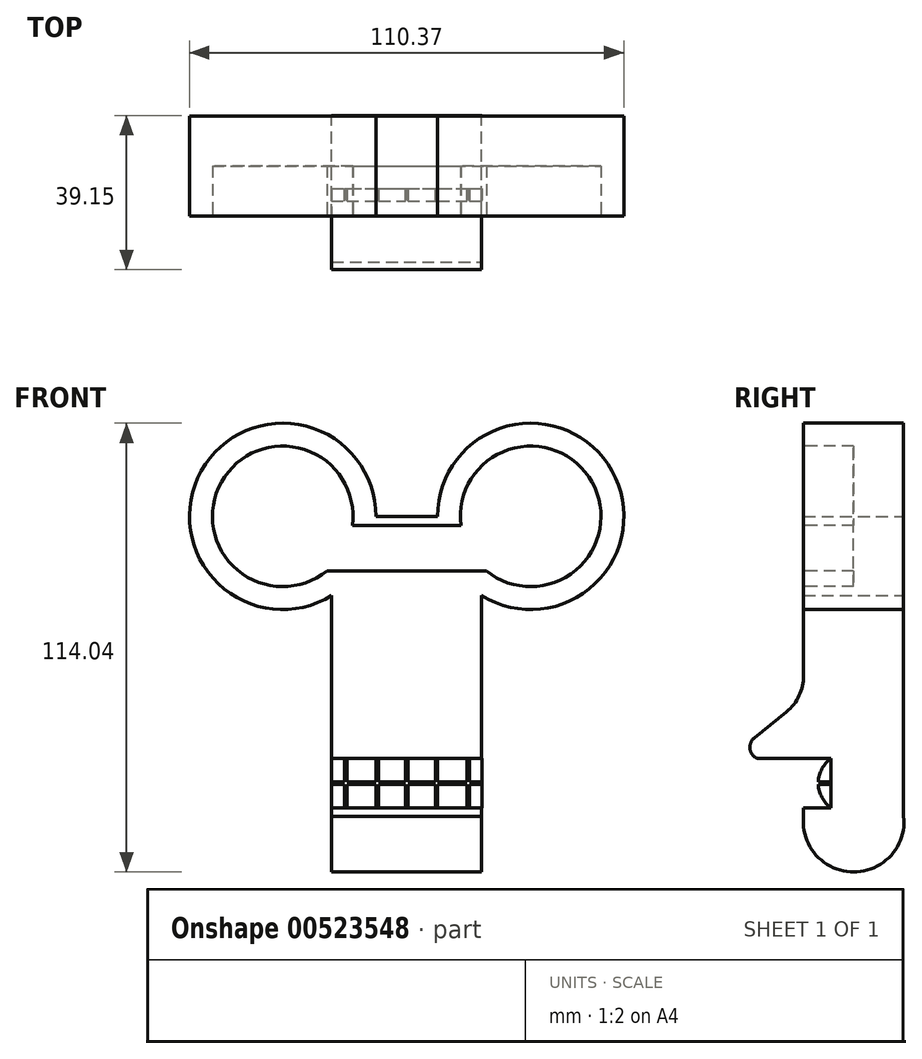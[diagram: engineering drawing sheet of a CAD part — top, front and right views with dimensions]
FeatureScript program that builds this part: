
annotation { "Feature Type Name" : "Feature", "Feature Type Description" : "" }
export const myFeature = defineFeature(function(context is Context, id is Id, definition is map)
    precondition{}
    {
        {
            var Q0;
            Q0=qCreatedBy(makeId("Front.planeOp"),FACE);
            var sketch = newSketch(context, id + "F0", { "sketchPlane" : qUnion([Q0])});
            skLineSegment(sketch, "E0.bottom", {"start": v(-13.77, 56.32) * mm, "end": v(1.87, 56.32) * mm});
            skLineSegment(sketch, "E0.top", {"start": v(-25, -19.88) * mm, "end": v(13.1, -19.88) * mm});
            skLineSegment(sketch, "E0.left", {"start": v(-25, 36.18) * mm, "end": v(-25, -19.88) * mm});
            skLineSegment(sketch, "E0.right", {"start": v(13.1, 36.17) * mm, "end": v(13.1, -19.88) * mm});
            skArc(sketch, "E1", {"start": v(-13.77, 56.32) * mm, "mid": v(-58.14, 67.85) * mm, "end": v(-25, 36.18) * mm});
            skArc(sketch, "E2", {"start": v(13.1, 36.17) * mm, "mid": v(46.23, 67.85) * mm, "end": v(1.87, 56.32) * mm});
            skPoint(sketch, "E3.orphan", {"position": v(-25, 56.32) * mm});
            skPoint(sketch, "E4.orphan", {"position": v(13.1, 56.32) * mm});
            skArc(sketch, "E5", {"start": v(-19.76, 54.02) * mm, "mid": v(-53.04, 65.01) * mm, "end": v(-26.2, 42.48) * mm});
            skArc(sketch, "E6", {"start": v(14.28, 42.48) * mm, "mid": v(41.14, 65.01) * mm, "end": v(7.85, 54.02) * mm});
            skLineSegment(sketch, "E7", {"start": v(-19.76, 54.02) * mm, "end": v(7.85, 54.02) * mm});
            skLineSegment(sketch, "E8", {"start": v(-26.2, 42.48) * mm, "end": v(14.28, 42.48) * mm});
            skSolve(sketch);
        }
        {
            var Q0;
            Q0 = qSketchRegion(id + "F0", true);
            var Q1;
            Q1=makeQuery(id+"F0.imprint","IMPRINT",FACE,{"disambiguationData":[TD([[makeQuery(id+"F0.imprint","IMPRINT",EDGE,{"derivedFrom":sQuery(id+"F0.wireOp",EDGE,"E5")}),1.0]])]});
            extrude(context, id + "F1", {"entities" : qUnion([Q0, Q1]), "depth" : 25.4 * mm, "offsetDistance" : 25.4 * mm});
        }
        {
            var Q0;
            Q0=makeQuery(id+"F1.opExtrude","SWEPT_FACE",FACE,{"disambiguationData":[OSD([sQuery(id+"F0.wireOp",EDGE,"E0.right")])]});
            var sketch = newSketch(context, id + "F2", { "sketchPlane" : qUnion([Q0])});
            skArc(sketch, "E9", {"start": v(-25.4, -19.88) * mm, "mid": v(-12.7, -34.04) * mm, "end": v(0, -19.88) * mm});
            skSolve(sketch);
        }
        {
            var Q0;
            Q0=makeQuery(id+"F2.imprint","IMPRINT",FACE,{"disambiguationData":[TD([[makeQuery(id+"F2.imprint","IMPRINT",EDGE,{"derivedFrom":sQuery(id+"F2.wireOp",EDGE,"E9")}),1.0]])]});
            var Q1;
            Q1=makeQuery(id+"F1.opExtrude","SWEPT_FACE",FACE,{"disambiguationData":[OSD([sQuery(id+"F0.wireOp",EDGE,"E0.left")])]});
            extrude(context, id + "F3", {"entities" : qUnion([Q0]), "operationType" : NewBodyOperationType.ADD, "endBound" : BoundingType.UP_TO_SURFACE, "oppositeDirection" : true, "depth" : 25.4 * mm, "endBoundEntityFace" : qUnion([Q1]), "offsetDistance" : 25.4 * mm});
        }
        {
            var Q0;
            {var subQ0=sQuery(id+"F0.wireOp",EDGE,"E0.right");Q0=makeQuery(id+"F3.boolean.opBoolean","MERGE",FACE,{"derivedFrom":[makeQuery(id+"F1.opExtrude","SWEPT_FACE",FACE,{"disambiguationData":[OSD([subQ0])]}),makeQuery(id+"F3.opExtrude","CAP_FACE",FACE,{"disambiguationData":[OSD([sQuery(id+"F0.wireOp",EDGE,"E0.top"),subQ0,sQuery(id+"F2.wireOp",EDGE,"E9")])],"isStart":true})]});}
            var sketch = newSketch(context, id + "F4", { "sketchPlane" : qUnion([Q0])});
            skLineSegment(sketch, "E10", {"start": v(-25.4, 10.2) * mm, "end": v(-37.94, 0) * mm});
            skArc(sketch, "E11", {"start": v(-37.94, 0) * mm, "mid": v(-39.04, -2.8) * mm, "end": v(-37.2, -5.18) * mm});
            skLineSegment(sketch, "E12", {"start": v(-37.2, -5.18) * mm, "end": v(-25.4, -5.18) * mm});
            skLineSegment(sketch, "E13.bottom", {"start": v(-25.4, -5.18) * mm, "end": v(-18.41, -5.18) * mm});
            skLineSegment(sketch, "E13.top", {"start": v(-25.4, -17.75) * mm, "end": v(-18.41, -17.75) * mm});
            skLineSegment(sketch, "E13.left", {"start": v(-25.4, -5.18) * mm, "end": v(-25.4, -17.75) * mm});
            skLineSegment(sketch, "E13.right", {"start": v(-18.41, -5.18) * mm, "end": v(-18.41, -17.75) * mm});
            skSolve(sketch);
        }
        {
            var Q0;
            {var subQ0=sQuery(id+"F4.wireOp",EDGE,"E10");Q0=makeQuery(id+"F4.imprint","IMPRINT",FACE,{"disambiguationData":[TD([[makeQuery(id+"F4.imprint","IMPRINT",EDGE,{"derivedFrom":subQ0}),1.0]])]});}
            var Q1;
            {var subQ0=sQuery(id+"F0.wireOp",EDGE,"E0.left");Q1=makeQuery(id+"F3.boolean.opBoolean","MERGE",FACE,{"derivedFrom":[makeQuery(id+"F1.opExtrude","SWEPT_FACE",FACE,{"disambiguationData":[OSD([subQ0])]}),makeQuery(id+"F3.opExtrude","CAP_FACE",FACE,{"disambiguationData":[OSD([subQ0])],"isStart":false})]});}
            extrude(context, id + "F5", {"entities" : qUnion([Q0]), "operationType" : NewBodyOperationType.ADD, "endBound" : BoundingType.UP_TO_SURFACE, "oppositeDirection" : true, "depth" : 25.4 * mm, "endBoundEntityFace" : qUnion([Q1]), "offsetDistance" : 25.4 * mm});
        }
        {
            var Q0;
            Q0=makeQuery(id+"F4.imprint","IMPRINT",FACE,{"disambiguationData":[TD([[makeQuery(id+"F4.imprint","IMPRINT",EDGE,{"derivedFrom":sQuery(id+"F4.wireOp",EDGE,"E13.bottom")}),-1.0]])]});
            extrude(context, id + "F6", {"entities" : qUnion([Q0]), "operationType" : NewBodyOperationType.REMOVE, "endBound" : BoundingType.THROUGH_ALL, "oppositeDirection" : true, "depth" : 25.4 * mm, "offsetDistance" : 25.4 * mm});
        }
        {
            var Q0;
            Q0=makeQuery(id+"F6.boolean.opBoolean","COPY",FACE,{"derivedFrom":makeQuery(id+"F6.opExtrude","SWEPT_FACE",FACE,{"disambiguationData":[OSD([sQuery(id+"F4.wireOp",EDGE,"E13.right")])]})});
            var sketch = newSketch(context, id + "F7", { "sketchPlane" : qUnion([Q0])});
            skLineSegment(sketch, "E14", {"start": v(-5.95, -5.18) * mm, "end": v(-5.95, -17.75) * mm, "construction": true});
            skSolve(sketch);
        }
        {
            var Q0;
            Q0=sQuery(id+"F7.wireOp",EDGE,"E14");
            cPlane(context, id + "F8", {"entities" : qUnion([Q0]), "cplaneType" : CPlaneType.LINE_ANGLE, "offset" : 25.4 * mm, "angle" : 0 * degree, "width" : 152.4 * mm, "height" : 152.4 * mm});
        }
        {
            var Q0;
            Q0=qCreatedBy(id+"F8.planeOp",FACE);
            var sketch = newSketch(context, id + "F9", { "sketchPlane" : qUnion([Q0])});
            skLineSegment(sketch, "E15", {"start": v(18.41, -5.18) * mm, "end": v(18.41, -17.75) * mm});
            skArc(sketch, "E16", {"start": v(18.41, -17.75) * mm, "mid": v(21.68, -11.47) * mm, "end": v(18.41, -5.18) * mm});
            skLineSegment(sketch, "E17.0.1", {"start": v(25.4, -17.75) * mm, "end": v(18.41, -17.75) * mm});
            skLineSegment(sketch, "E17.0.3", {"start": v(18.41, -17.75) * mm, "end": v(25.4, -17.75) * mm});
            skLineSegment(sketch, "E18", {"start": v(21.68, -11.47) * mm, "end": v(21.68, -17.75) * mm, "construction": true});
            skSolve(sketch);
        }
        {
            var Q0;
            Q0=makeQuery(id+"F9.imprint","IMPRINT",FACE,{"disambiguationData":[TD([[makeQuery(id+"F9.imprint","IMPRINT",EDGE,{"derivedFrom":sQuery(id+"F9.wireOp",EDGE,"E15")}),1.0]])]});
            extrude(context, id + "F10", {"entities" : qUnion([Q0]), "operationType" : NewBodyOperationType.ADD, "endBound" : BoundingType.SYMMETRIC, "depth" : 38.3 * mm, "offsetDistance" : 25.4 * mm});
        }
        {
            var Q0;
            {var subQ0=sQuery(id+"F0.wireOp",EDGE,"E1");var subQ1=sQuery(id+"F0.wireOp",EDGE,"E0.left");var subQ2=sQuery(id+"F0.wireOp",EDGE,"E0.right");var subQ3=sQuery(id+"F0.wireOp",EDGE,"E0.bottom");var subQ4=sQuery(id+"F0.wireOp",EDGE,"E2");var subQ6=sQuery(id+"F0.wireOp",EDGE,"E0.top");Q0=makeQuery(id+"F5.boolean.opBoolean","SPLIT",FACE,{"disambiguationData":[TD([makeQuery(id+"F1.opExtrude","SWEPT_FACE",FACE,{"disambiguationData":[OSD([subQ3])]})])],"derivedFrom":makeQuery(id+"F1.opExtrude","CAP_FACE",FACE,{"disambiguationData":[OSD([subQ3,subQ6,subQ1,subQ2,subQ0,subQ4])],"isStart":false})});}
            var sketch = newSketch(context, id + "F11", { "sketchPlane" : qUnion([Q0])});
            skLineSegment(sketch, "E19.bottom", {"start": v(-19.72, 56.32) * mm, "end": v(-19.6, 56.32) * mm});
            skLineSegment(sketch, "E19.top", {"start": v(-25, -19.88) * mm, "end": v(13.1, -19.88) * mm});
            skLineSegment(sketch, "E19.left", {"start": v(-25, 43.7) * mm, "end": v(-25, -19.88) * mm});
            skLineSegment(sketch, "E19.right", {"start": v(13.1, 43.69) * mm, "end": v(13.1, -19.88) * mm});
            skPoint(sketch, "E20.orphan", {"position": v(-25, 56.32) * mm});
            skPoint(sketch, "E21.orphan", {"position": v(13.1, 56.32) * mm});
            skArc(sketch, "E22", {"start": v(-19.76, 54.02) * mm, "mid": v(-53.04, 65.01) * mm, "end": v(-26.2, 42.48) * mm});
            skArc(sketch, "E23", {"start": v(14.28, 42.48) * mm, "mid": v(41.14, 65.01) * mm, "end": v(7.85, 54.02) * mm});
            skLineSegment(sketch, "E24", {"start": v(-19.76, 54.02) * mm, "end": v(7.85, 54.02) * mm});
            skLineSegment(sketch, "E25", {"start": v(-26.2, 42.48) * mm, "end": v(14.28, 42.48) * mm});
            skLineSegment(sketch, "E26.trimOffspring", {"start": v(7.7, 56.32) * mm, "end": v(7.81, 56.32) * mm});
            skSolve(sketch);
        }
        {
            var Q0;
            {var subQ0=sQuery(id+"F11.wireOp",EDGE,"E24");Q0=makeQuery(id+"F11.imprint","IMPRINT",FACE,{"disambiguationData":[TD([[makeQuery(id+"F11.imprint","IMPRINT",EDGE,{"derivedFrom":subQ0}),-1.0]])]});}
            extrude(context, id + "F12", {"entities" : qUnion([Q0]), "operationType" : NewBodyOperationType.REMOVE, "oppositeDirection" : true, "depth" : 12.7 * mm, "offsetDistance" : 25.4 * mm});
        }
        {
            var Q0;
            Q0=sQuery(id+"F9.wireOp",EDGE,"E18");
            cPlane(context, id + "F13", {"entities" : qUnion([Q0]), "cplaneType" : CPlaneType.LINE_ANGLE, "offset" : 25.4 * mm, "angle" : 90 * degree, "oppositeDirection" : true, "width" : 152.4 * mm, "height" : 152.4 * mm});
        }
        {
            var Q0;
            Q0=qCreatedBy(id+"F13.planeOp",FACE);
            var sketch = newSketch(context, id + "F14", { "sketchPlane" : qUnion([Q0])});
            skLineSegment(sketch, "E27", {"start": v(-25.1, -11.47) * mm, "end": v(13.2, -11.47) * mm});
            skLineSegment(sketch, "E28", {"start": v(1.63, -11.47) * mm, "end": v(1.63, -11.47) * mm});
            skLineSegment(sketch, "E29.bottom", {"start": v(-21.75, -5.18) * mm, "end": v(-21.16, -5.18) * mm});
            skLineSegment(sketch, "E29.top", {"start": v(-21.75, -17.75) * mm, "end": v(-21.16, -17.75) * mm});
            skLineSegment(sketch, "E29.left", {"start": v(-21.75, -5.18) * mm, "end": v(-21.75, -17.75) * mm});
            skLineSegment(sketch, "E29.right", {"start": v(-21.16, -5.18) * mm, "end": v(-21.16, -17.75) * mm});
            skPoint(sketch, "E29.middle", {"position": v(-21.46, -11.47) * mm});
            skLineSegment(sketch, "E30.bottom", {"start": v(-13.69, -5.18) * mm, "end": v(-13.1, -5.18) * mm});
            skLineSegment(sketch, "E30.top", {"start": v(-13.69, -17.75) * mm, "end": v(-13.1, -17.75) * mm});
            skLineSegment(sketch, "E30.left", {"start": v(-13.69, -5.18) * mm, "end": v(-13.69, -17.75) * mm});
            skLineSegment(sketch, "E30.right", {"start": v(-13.1, -5.18) * mm, "end": v(-13.1, -17.75) * mm});
            skPoint(sketch, "E30.middle", {"position": v(-13.39, -11.47) * mm});
            skLineSegment(sketch, "E31.bottom", {"start": v(-6.25, -5.18) * mm, "end": v(-5.65, -5.18) * mm});
            skLineSegment(sketch, "E31.top", {"start": v(-6.25, -17.75) * mm, "end": v(-5.65, -17.75) * mm});
            skLineSegment(sketch, "E31.left", {"start": v(-6.25, -5.18) * mm, "end": v(-6.25, -17.75) * mm});
            skLineSegment(sketch, "E31.right", {"start": v(-5.65, -5.18) * mm, "end": v(-5.65, -17.75) * mm});
            skPoint(sketch, "E31.middle", {"position": v(-5.95, -11.47) * mm});
            skLineSegment(sketch, "E32.bottom", {"start": v(1.33, -5.18) * mm, "end": v(1.93, -5.18) * mm});
            skLineSegment(sketch, "E32.top", {"start": v(1.33, -17.75) * mm, "end": v(1.93, -17.75) * mm});
            skLineSegment(sketch, "E32.left", {"start": v(1.33, -5.18) * mm, "end": v(1.33, -17.75) * mm});
            skLineSegment(sketch, "E32.right", {"start": v(1.93, -5.18) * mm, "end": v(1.93, -17.75) * mm});
            skPoint(sketch, "E32.middle", {"position": v(1.63, -11.47) * mm});
            skLineSegment(sketch, "E33.bottom", {"start": v(9.35, -5.18) * mm, "end": v(9.95, -5.18) * mm});
            skLineSegment(sketch, "E33.top", {"start": v(9.35, -17.75) * mm, "end": v(9.95, -17.75) * mm});
            skLineSegment(sketch, "E33.left", {"start": v(9.35, -5.18) * mm, "end": v(9.35, -17.75) * mm});
            skLineSegment(sketch, "E33.right", {"start": v(9.95, -5.18) * mm, "end": v(9.95, -17.75) * mm});
            skPoint(sketch, "E33.middle", {"position": v(9.65, -11.47) * mm});
            skPoint(sketch, "E34.orphan", {"position": v(-21.46, -5.18) * mm});
            skPoint(sketch, "E35.MirrorCS.end.orphan", {"position": v(-21.46, -17.75) * mm});
            skPoint(sketch, "E36.orphan", {"position": v(-13.53, -17.75) * mm});
            skPoint(sketch, "E37.MirrorCS.start.orphan", {"position": v(-13.53, -5.18) * mm});
            skPoint(sketch, "E38.orphan", {"position": v(1.63, -17.75) * mm});
            skPoint(sketch, "E39.orphan", {"position": v(1.63, -5.18) * mm});
            skPoint(sketch, "E40.orphan", {"position": v(9.56, -5.18) * mm});
            skPoint(sketch, "E41.end.orphan", {"position": v(9.56, -17.75) * mm});
            skLineSegment(sketch, "E42.bottom", {"start": v(-25.1, -11.17) * mm, "end": v(13.2, -11.17) * mm});
            skLineSegment(sketch, "E42.top", {"start": v(-25.1, -11.76) * mm, "end": v(13.2, -11.76) * mm});
            skLineSegment(sketch, "E42.left", {"start": v(-25.1, -11.17) * mm, "end": v(-25.1, -11.76) * mm});
            skLineSegment(sketch, "E42.right", {"start": v(13.2, -11.17) * mm, "end": v(13.2, -11.76) * mm});
            skSolve(sketch);
        }
        {
            var Q0;
            Q0 = qSketchRegion(id + "F14", true);
            var Q1;
            {var subQ0=sQuery(id+"F0.wireOp",EDGE,"E1");var subQ1=sQuery(id+"F0.wireOp",EDGE,"E0.left");var subQ2=sQuery(id+"F0.wireOp",EDGE,"E0.right");var subQ3=sQuery(id+"F0.wireOp",EDGE,"E0.bottom");var subQ4=sQuery(id+"F0.wireOp",EDGE,"E2");var subQ6=sQuery(id+"F0.wireOp",EDGE,"E0.top");Q1=makeQuery(id+"F5.boolean.opBoolean","SPLIT",FACE,{"disambiguationData":[TD([makeQuery(id+"F1.opExtrude","SWEPT_FACE",FACE,{"disambiguationData":[OSD([subQ3])]})])],"derivedFrom":makeQuery(id+"F1.opExtrude","CAP_FACE",FACE,{"disambiguationData":[OSD([subQ3,subQ6,subQ1,subQ2,subQ0,subQ4])],"isStart":false})});}
            extrude(context, id + "F15", {"entities" : qUnion([Q0]), "operationType" : NewBodyOperationType.REMOVE, "oppositeDirection" : true, "depth" : 3.25 * mm, "endBoundEntityFace" : qUnion([Q1]), "offsetDistance" : 25.4 * mm});
        }
        {
            var Q0;
            Q0=makeQuery(id+"F5.opExtrude","SWEPT_EDGE",EDGE,{"disambiguationData":[OSD([sQuery(id+"F0.wireOp",EDGE,"E0.right"),sQuery(id+"F4.wireOp",EDGE,"E10")])]});
            fillet(context, id + "F16", {"entities" : qUnion([Q0]), "radius" : 11.84 * mm, "tangentPropagation" : true, "allowEdgeOverflow" : false});
        }
    });
